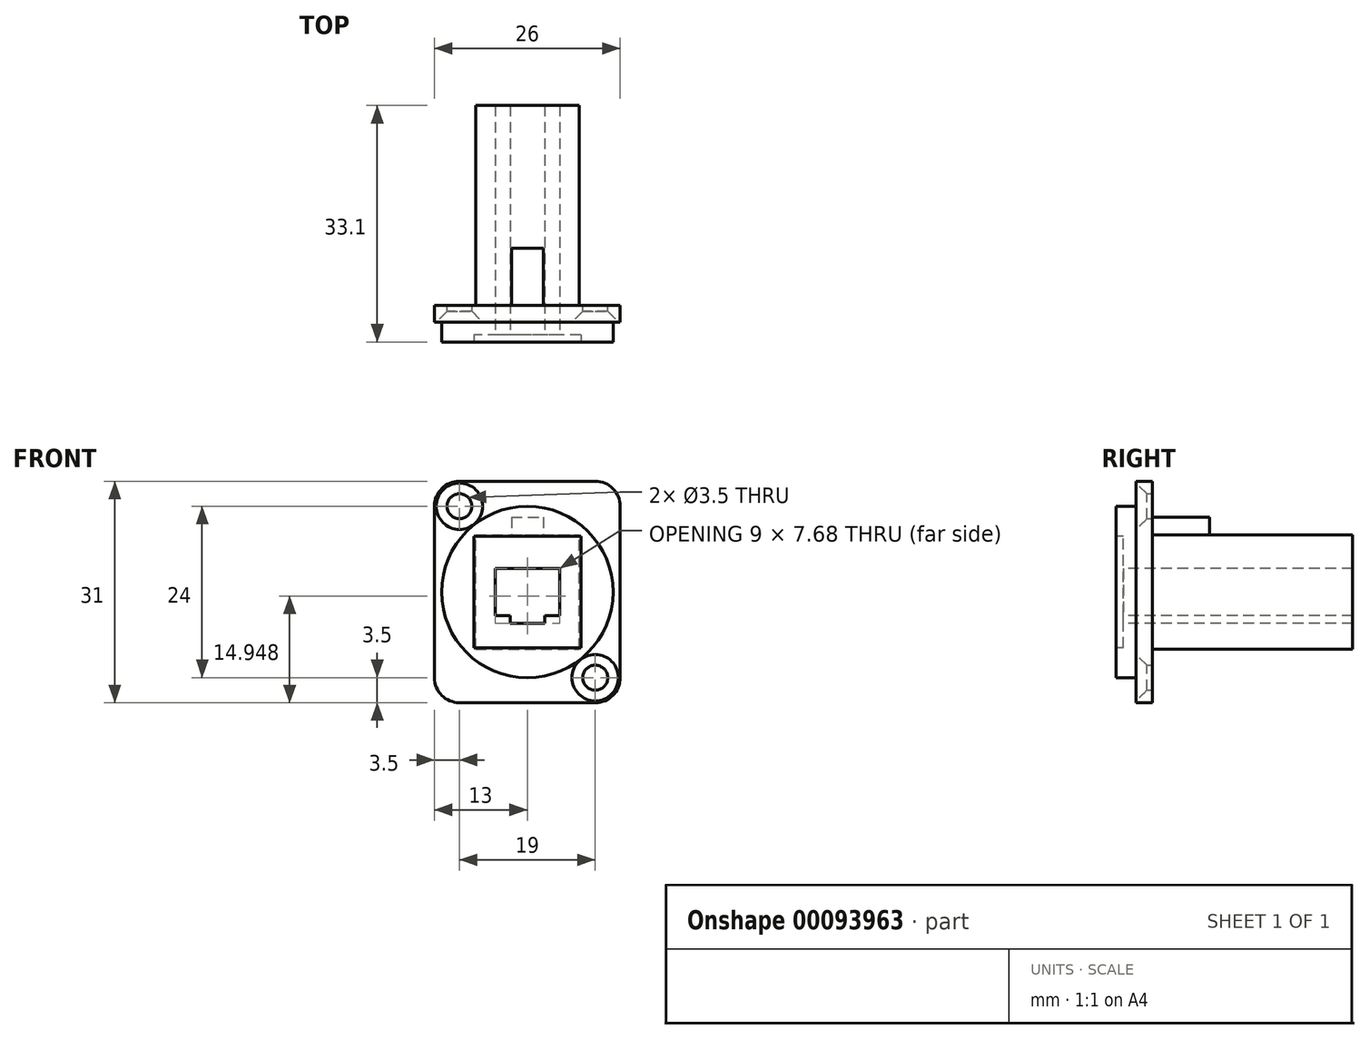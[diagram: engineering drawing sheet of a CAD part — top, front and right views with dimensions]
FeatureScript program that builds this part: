
annotation { "Feature Type Name" : "Feature", "Feature Type Description" : "" }
export const myFeature = defineFeature(function(context is Context, id is Id, definition is map)
    precondition{}
    {
        {
            var Q0;
            Q0=qCreatedBy(makeId("Front.planeOp"),FACE);
            var sketch = newSketch(context, id + "F0", { "sketchPlane" : qUnion([Q0])});
            skLineSegment(sketch, "E0.bottom", {"start": v(9.5, 15.5) * mm, "end": v(-9.5, 15.5) * mm});
            skLineSegment(sketch, "E0.top", {"start": v(9.5, -15.5) * mm, "end": v(-9.5, -15.5) * mm});
            skLineSegment(sketch, "E0.left", {"start": v(13, 12) * mm, "end": v(13, -12) * mm});
            skLineSegment(sketch, "E0.right", {"start": v(-13, 12) * mm, "end": v(-13, -12) * mm});
            skPoint(sketch, "E0.middle", {"position": v(0, 0) * mm});
            skCircle(sketch, "E1", {"center": v(-9.5, 12) * mm, "radius": 1.75 * mm});
            skCircle(sketch, "E2", {"center": v(9.5, -12) * mm, "radius": 1.75 * mm});
            skCircle(sketch, "E3", {"center": v(0, 0) * mm, "radius": 12 * mm});
            skPoint(sketch, "E4.visualSharp", {"position": v(-13, 15.5) * mm});
            skArc(sketch, "E4.filletArc", {"start": v(-9.5, 15.5) * mm, "mid": v(-11.97, 14.47) * mm, "end": v(-13, 12) * mm});
            skPoint(sketch, "E5.visualSharp", {"position": v(13, 15.5) * mm});
            skArc(sketch, "E5.filletArc", {"start": v(13, 12) * mm, "mid": v(11.97, 14.47) * mm, "end": v(9.5, 15.5) * mm});
            skPoint(sketch, "E6.visualSharp", {"position": v(13, -15.5) * mm});
            skArc(sketch, "E6.filletArc", {"start": v(9.5, -15.5) * mm, "mid": v(11.97, -14.47) * mm, "end": v(13, -12) * mm});
            skPoint(sketch, "E7.visualSharp", {"position": v(-13, -15.5) * mm});
            skArc(sketch, "E7.filletArc", {"start": v(-13, -12) * mm, "mid": v(-11.97, -14.47) * mm, "end": v(-9.5, -15.5) * mm});
            skSolve(sketch);
        }
        {
            var Q0;
            Q0 = qSketchRegion(id + "F0", true);
            var Q1;
            Q1=makeQuery(id+"F0.imprint","IMPRINT",FACE,{"disambiguationData":[TD([[makeQuery(id+"F0.imprint","IMPRINT",EDGE,{"derivedFrom":sQuery(id+"F0.wireOp",EDGE,"E3")}),1.0]])]});
            extrude(context, id + "F1", {"entities" : qUnion([Q0, Q1]), "depth" : 2.3 * mm});
        }
        {
            var Q0;
            Q0=makeQuery(id+"F0.imprint","IMPRINT",FACE,{"disambiguationData":[TD([[makeQuery(id+"F0.imprint","IMPRINT",EDGE,{"derivedFrom":sQuery(id+"F0.wireOp",EDGE,"E3")}),1.0]])]});
            extrude(context, id + "F2", {"entities" : qUnion([Q0]), "operationType" : NewBodyOperationType.ADD, "depth" : 5.1 * mm});
        }
        {
            var Q0;
            Q0=makeQuery(id+"F2.opExtrude","CAP_FACE",FACE,{"disambiguationData":[OSD([sQuery(id+"F0.wireOp",EDGE,"E3")])],"isStart":false});
            var sketch = newSketch(context, id + "F3", { "sketchPlane" : qUnion([Q0])});
            skLineSegment(sketch, "E8.bottom", {"start": v(7.49, -7.82) * mm, "end": v(-7.49, -7.82) * mm});
            skLineSegment(sketch, "E8.top", {"start": v(7.49, 7.82) * mm, "end": v(-7.49, 7.82) * mm});
            skLineSegment(sketch, "E8.left", {"start": v(7.49, -7.82) * mm, "end": v(7.49, 7.82) * mm});
            skLineSegment(sketch, "E8.right", {"start": v(-7.49, -7.82) * mm, "end": v(-7.49, 7.82) * mm});
            skPoint(sketch, "E8.middle", {"position": v(0, 0) * mm});
            skLineSegment(sketch, "E9.bottom", {"start": v(4.5, 3.29) * mm, "end": v(-4.5, 3.29) * mm});
            skLineSegment(sketch, "E9.top", {"start": v(4.5, -3.29) * mm, "end": v(-4.5, -3.29) * mm});
            skLineSegment(sketch, "E9.left", {"start": v(4.5, 3.29) * mm, "end": v(4.5, -3.29) * mm});
            skLineSegment(sketch, "E9.right", {"start": v(-4.5, 3.29) * mm, "end": v(-4.5, -3.29) * mm});
            skLineSegment(sketch, "E10.bottom", {"start": v(2.42, -4.4) * mm, "end": v(-2.42, -4.4) * mm});
            skLineSegment(sketch, "E10.top", {"start": v(2.42, -2.18) * mm, "end": v(-2.42, -2.18) * mm});
            skLineSegment(sketch, "E10.left", {"start": v(2.42, -4.4) * mm, "end": v(2.42, -2.18) * mm});
            skLineSegment(sketch, "E10.right", {"start": v(-2.42, -4.4) * mm, "end": v(-2.42, -2.18) * mm});
            skPoint(sketch, "E10.middle", {"position": v(0, -3.29) * mm});
            skSolve(sketch);
        }
        {
            var Q0;
            Q0=makeQuery(id+"F3.imprint","IMPRINT",FACE,{"disambiguationData":[TD([[makeQuery(id+"F3.imprint","IMPRINT",EDGE,{"derivedFrom":sQuery(id+"F3.wireOp",EDGE,"E9.bottom")}),1.0]])]});
            var Q1;
            {var subQ5=sQuery(id+"F3.wireOp",EDGE,"E10.top");Q1=makeQuery(id+"F3.imprint","IMPRINT",FACE,{"disambiguationData":[TD([[makeQuery(id+"F3.imprint","IMPRINT",EDGE,{"derivedFrom":subQ5}),1.0]])]});}
            var Q2;
            {var subQ5=sQuery(id+"F3.wireOp",EDGE,"E10.bottom");Q2=makeQuery(id+"F3.imprint","IMPRINT",FACE,{"disambiguationData":[TD([[makeQuery(id+"F3.imprint","IMPRINT",EDGE,{"derivedFrom":subQ5}),-1.0]])]});}
            var Q3;
            Q3=makeQuery(id+"F3.imprint","IMPRINT",FACE,{"disambiguationData":[TD([[makeQuery(id+"F3.imprint","IMPRINT",EDGE,{"derivedFrom":sQuery(id+"F3.wireOp",EDGE,"E8.bottom")}),-1.0]])]});
            extrude(context, id + "F4", {"entities" : qUnion([Q0, Q1, Q2, Q3]), "operationType" : NewBodyOperationType.REMOVE, "oppositeDirection" : true, "depth" : 1 * mm});
        }
        {
            var Q0;
            Q0=makeQuery(id+"F3.imprint","IMPRINT",FACE,{"disambiguationData":[TD([[makeQuery(id+"F3.imprint","IMPRINT",EDGE,{"derivedFrom":sQuery(id+"F3.wireOp",EDGE,"E9.bottom")}),1.0]])]});
            var Q1;
            {var subQ5=sQuery(id+"F3.wireOp",EDGE,"E10.top");Q1=makeQuery(id+"F3.imprint","IMPRINT",FACE,{"disambiguationData":[TD([[makeQuery(id+"F3.imprint","IMPRINT",EDGE,{"derivedFrom":subQ5}),1.0]])]});}
            var Q2;
            {var subQ5=sQuery(id+"F3.wireOp",EDGE,"E10.bottom");Q2=makeQuery(id+"F3.imprint","IMPRINT",FACE,{"disambiguationData":[TD([[makeQuery(id+"F3.imprint","IMPRINT",EDGE,{"derivedFrom":subQ5}),-1.0]])]});}
            extrude(context, id + "F5", {"entities" : qUnion([Q0, Q1, Q2]), "operationType" : NewBodyOperationType.REMOVE, "oppositeDirection" : true, "depth" : 3 * mm});
        }
        {
            var Q0;
            Q0=makeQuery(id+"F1.opExtrude","CAP_EDGE",EDGE,{"disambiguationData":[OSD([sQuery(id+"F0.wireOp",EDGE,"E1")])],"isStart":false});
            var Q1;
            Q1=makeQuery(id+"F1.opExtrude","CAP_EDGE",EDGE,{"disambiguationData":[OSD([sQuery(id+"F0.wireOp",EDGE,"E2")])],"isStart":false});
            chamfer(context, id + "F6", {"entities" : qUnion([Q0, Q1]), "width" : 1.5 * mm, "tangentPropagation" : true});
        }
        {
            var Q0;
            Q0=makeQuery(id+"F1.opExtrude","CAP_FACE",FACE,{"disambiguationData":[OSD([sQuery(id+"F0.wireOp",EDGE,"E0.bottom"),sQuery(id+"F0.wireOp",EDGE,"E0.top"),sQuery(id+"F0.wireOp",EDGE,"E0.left"),sQuery(id+"F0.wireOp",EDGE,"E0.right"),sQuery(id+"F0.wireOp",EDGE,"E1"),sQuery(id+"F0.wireOp",EDGE,"E2"),sQuery(id+"F0.wireOp",EDGE,"E4.filletArc"),sQuery(id+"F0.wireOp",EDGE,"E5.filletArc"),sQuery(id+"F0.wireOp",EDGE,"E6.filletArc"),sQuery(id+"F0.wireOp",EDGE,"E7.filletArc")])],"isStart":true});
            var sketch = newSketch(context, id + "F7", { "sketchPlane" : qUnion([Q0])});
            skLineSegment(sketch, "E11.bottom", {"start": v(7.25, -8) * mm, "end": v(-7.25, -8) * mm});
            skLineSegment(sketch, "E11.top", {"start": v(7.25, 8) * mm, "end": v(-7.25, 8) * mm});
            skLineSegment(sketch, "E11.left", {"start": v(7.25, -8) * mm, "end": v(7.25, 8) * mm});
            skLineSegment(sketch, "E11.right", {"start": v(-7.25, -8) * mm, "end": v(-7.25, 8) * mm});
            skPoint(sketch, "E11.middle", {"position": v(0, 0) * mm});
            skPoint(sketch, "E12.middle", {"position": v(0, 8) * mm});
            skPoint(sketch, "E12.top.end.orphan", {"position": v(-3.1, 6.1) * mm});
            skPoint(sketch, "E13.orphan", {"position": v(3.1, 6.1) * mm});
            skPoint(sketch, "E12.bottom.end.orphan", {"position": v(-3.1, 9.9) * mm});
            skPoint(sketch, "E12.left.start.orphan", {"position": v(3.1, 9.9) * mm});
            skSolve(sketch);
        }
        {
            var Q0;
            Q0 = qSketchRegion(id + "F7", true);
            extrude(context, id + "F8", {"entities" : qUnion([Q0]), "operationType" : NewBodyOperationType.ADD, "depth" : 28 * mm});
        }
        {
            var Q0;
            Q0=makeQuery(id+"F1.opExtrude","CAP_FACE",FACE,{"disambiguationData":[OSD([sQuery(id+"F0.wireOp",EDGE,"E0.bottom"),sQuery(id+"F0.wireOp",EDGE,"E0.top"),sQuery(id+"F0.wireOp",EDGE,"E0.left"),sQuery(id+"F0.wireOp",EDGE,"E0.right"),sQuery(id+"F0.wireOp",EDGE,"E1"),sQuery(id+"F0.wireOp",EDGE,"E2"),sQuery(id+"F0.wireOp",EDGE,"E4.filletArc"),sQuery(id+"F0.wireOp",EDGE,"E5.filletArc"),sQuery(id+"F0.wireOp",EDGE,"E6.filletArc"),sQuery(id+"F0.wireOp",EDGE,"E7.filletArc")])],"isStart":true});
            var sketch = newSketch(context, id + "F9", { "sketchPlane" : qUnion([Q0])});
            skLineSegment(sketch, "E14.bottom", {"start": v(2.22, 10.45) * mm, "end": v(-2.22, 10.45) * mm});
            skLineSegment(sketch, "E14.top", {"start": v(2.22, 5.55) * mm, "end": v(-2.22, 5.55) * mm});
            skLineSegment(sketch, "E14.left", {"start": v(2.22, 10.45) * mm, "end": v(2.22, 5.55) * mm});
            skLineSegment(sketch, "E14.right", {"start": v(-2.22, 10.45) * mm, "end": v(-2.22, 5.55) * mm});
            skPoint(sketch, "E14.middle", {"position": v(0, 8) * mm});
            skSolve(sketch);
        }
        {
            var Q0;
            Q0 = qSketchRegion(id + "F9", true);
            extrude(context, id + "F10", {"entities" : qUnion([Q0]), "operationType" : NewBodyOperationType.ADD, "depth" : 8 * mm});
        }
        {
            var Q0;
            Q0=makeQuery(id+"F5.boolean.opBoolean","COPY",FACE,{"derivedFrom":makeQuery(id+"F5.opExtrude","CAP_FACE",FACE,{"disambiguationData":[OSD([sQuery(id+"F3.wireOp",EDGE,"E9.bottom"),sQuery(id+"F3.wireOp",EDGE,"E9.top"),sQuery(id+"F3.wireOp",EDGE,"E9.left"),sQuery(id+"F3.wireOp",EDGE,"E9.right"),sQuery(id+"F3.wireOp",EDGE,"E10.bottom"),sQuery(id+"F3.wireOp",EDGE,"E10.left"),sQuery(id+"F3.wireOp",EDGE,"E10.right")])],"isStart":false})});
            var Q1;
            Q1=makeQuery(id+"F1.opExtrude","SWEPT_BODY",BODY,{"disambiguationData":[OSD([sQuery(id+"F0.wireOp",EDGE,"E0.bottom"),sQuery(id+"F0.wireOp",EDGE,"E0.top"),sQuery(id+"F0.wireOp",EDGE,"E0.left"),sQuery(id+"F0.wireOp",EDGE,"E0.right"),sQuery(id+"F0.wireOp",EDGE,"E1"),sQuery(id+"F0.wireOp",EDGE,"E2"),sQuery(id+"F0.wireOp",EDGE,"E4.filletArc"),sQuery(id+"F0.wireOp",EDGE,"E5.filletArc"),sQuery(id+"F0.wireOp",EDGE,"E6.filletArc"),sQuery(id+"F0.wireOp",EDGE,"E7.filletArc")])]});
            extrude(context, id + "F11", {"entities" : qUnion([Q0]), "operationType" : NewBodyOperationType.REMOVE, "endBound" : BoundingType.UP_TO_BODY, "oppositeDirection" : true, "endBoundEntityBody" : qUnion([Q1]), "depth" : 25 * mm});
        }
    });
